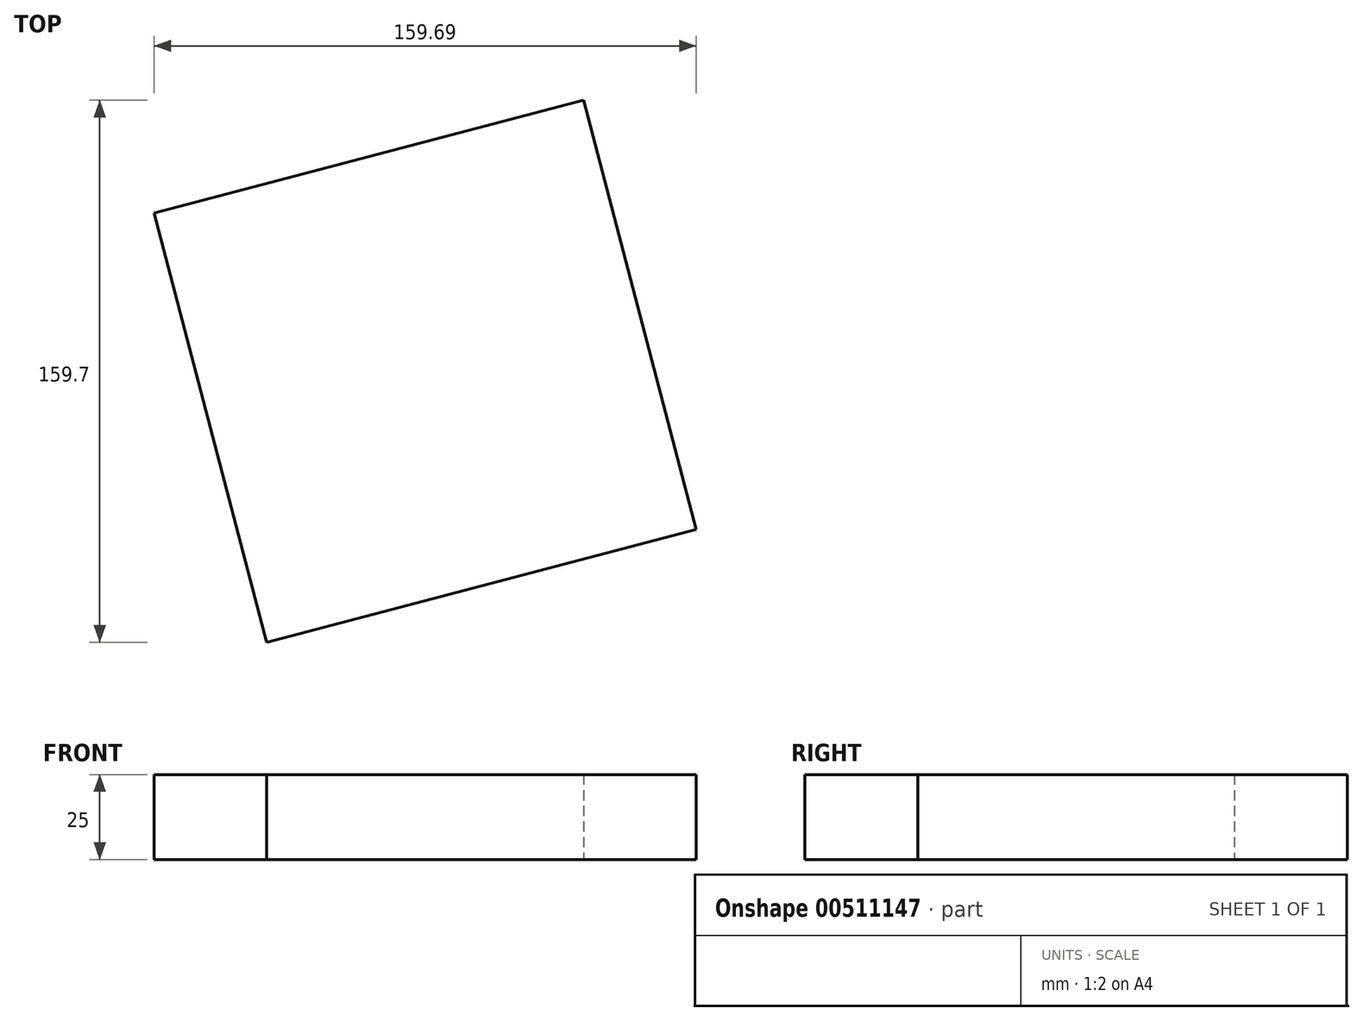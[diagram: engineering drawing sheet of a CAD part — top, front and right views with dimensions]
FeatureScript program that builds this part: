
annotation { "Feature Type Name" : "Feature", "Feature Type Description" : "" }
export const myFeature = defineFeature(function(context is Context, id is Id, definition is map)
    precondition{}
    {
        {
            var Q0;
            Q0=qCreatedBy(makeId("Top.planeOp"),FACE);
            var sketch = newSketch(context, id + "F0", { "sketchPlane" : qUnion([Q0])});
            skCircle(sketch, "E0.cCircle", {"center": v(2.71, 0) * mm, "radius": 92.46 * mm, "construction": true});
            skLineSegment(sketch, "E0.0", {"start": v(-43.9, -79.85) * mm, "end": v(-77.13, 46.61) * mm});
            skLineSegment(sketch, "E0.1", {"start": v(-77.13, 46.61) * mm, "end": v(49.33, 79.85) * mm});
            skLineSegment(sketch, "E0.2", {"start": v(49.33, 79.85) * mm, "end": v(82.56, -46.61) * mm});
            skLineSegment(sketch, "E0.3", {"start": v(82.56, -46.61) * mm, "end": v(-43.9, -79.85) * mm});
            skPoint(sketch, "E1", {"position": v(-7.67, 0) * mm});
            skSolve(sketch);
        }
        {
            var Q0;
            Q0 = qSketchRegion(id + "F0", true);
            extrude(context, id + "F1", {"entities" : qUnion([Q0]), "depth" : 25 * mm});
        }
        {
            var Q0;
            Q0=qCreatedBy(makeId("Top.planeOp"),FACE);
            var Q1;
            Q1 = qBodyType(qCreatedBy(id + "F3" ,EDGE), BodyType.WIRE);
            cPlane(context, id + "F2", {"entities" : qUnion([Q0, Q1]), "cplaneType" : CPlaneType.OFFSET, "offset" : 100 * mm, "width" : 150 * mm, "height" : 150 * mm});
        }
    });
